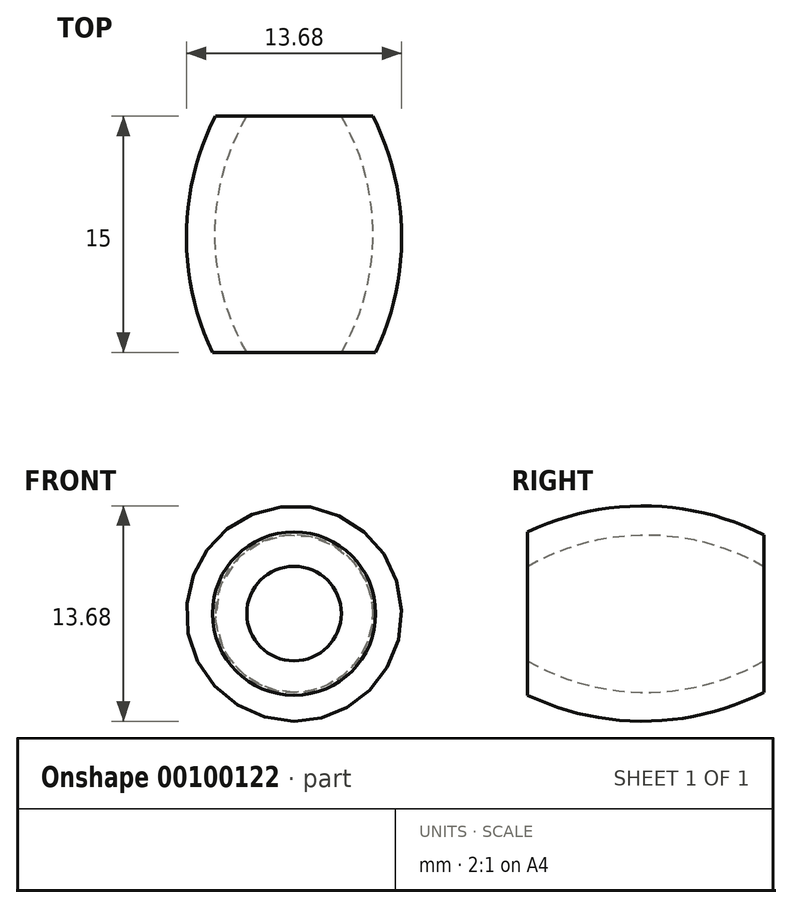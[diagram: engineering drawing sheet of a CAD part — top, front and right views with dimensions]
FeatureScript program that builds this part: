
annotation { "Feature Type Name" : "Feature", "Feature Type Description" : "" }
export const myFeature = defineFeature(function(context is Context, id is Id, definition is map)
    precondition{}
    {
        {
            var Q0;
            Q0=qCreatedBy(makeId("Right.planeOp"),FACE);
            var sketch = newSketch(context, id + "F0", { "sketchPlane" : qUnion([Q0])});
            skLineSegment(sketch, "E0", {"start": v(0, 0) * mm, "end": v(0, 3) * mm});
            skLineSegment(sketch, "E1", {"start": v(15, 3) * mm, "end": v(15, -3) * mm});
            skLineSegment(sketch, "E2", {"start": v(0, -3) * mm, "end": v(0, 3) * mm});
            skLineSegment(sketch, "E3", {"start": v(0, 3) * mm, "end": v(0, -3) * mm});
            skArc(sketch, "E4", {"start": v(15, 3) * mm, "mid": v(7.5, 5) * mm, "end": v(0, 3) * mm});
            skArc(sketch, "E5", {"start": v(0, -3) * mm, "mid": v(7.5, -5) * mm, "end": v(15, -3) * mm});
            skLineSegment(sketch, "E6.left", {"start": v(0, -5.19) * mm, "end": v(0, 5.19) * mm});
            skLineSegment(sketch, "E6.right", {"start": v(15, -5) * mm, "end": v(15, 5) * mm});
            skArc(sketch, "E7", {"start": v(15, 5) * mm, "mid": v(7.52, 6.84) * mm, "end": v(0, 5.19) * mm});
            skArc(sketch, "E8", {"start": v(0, -5.19) * mm, "mid": v(7.52, -6.84) * mm, "end": v(15, -5) * mm});
            skLineSegment(sketch, "E9", {"start": v(0, 0) * mm, "end": v(15, 0) * mm});
            skSolve(sketch);
        }
        {
            var Q0;
            {var subQ0=sQuery(id+"F0.wireOp",EDGE,"E4");Q0=makeQuery(id+"F0.imprint","IMPRINT",FACE,{"disambiguationData":[TD([[makeQuery(id+"F0.imprint","IMPRINT",EDGE,{"derivedFrom":subQ0}),-1.0]])]});}
            var Q1;
            Q1=sQuery(id+"F0.wireOp",EDGE,"E9");
            revolve(context, id + "F1", {"entities" : qUnion([Q0]), "axis" : qUnion([Q1]), "revolveType" : RevolveType.FULL});
        }
    });
